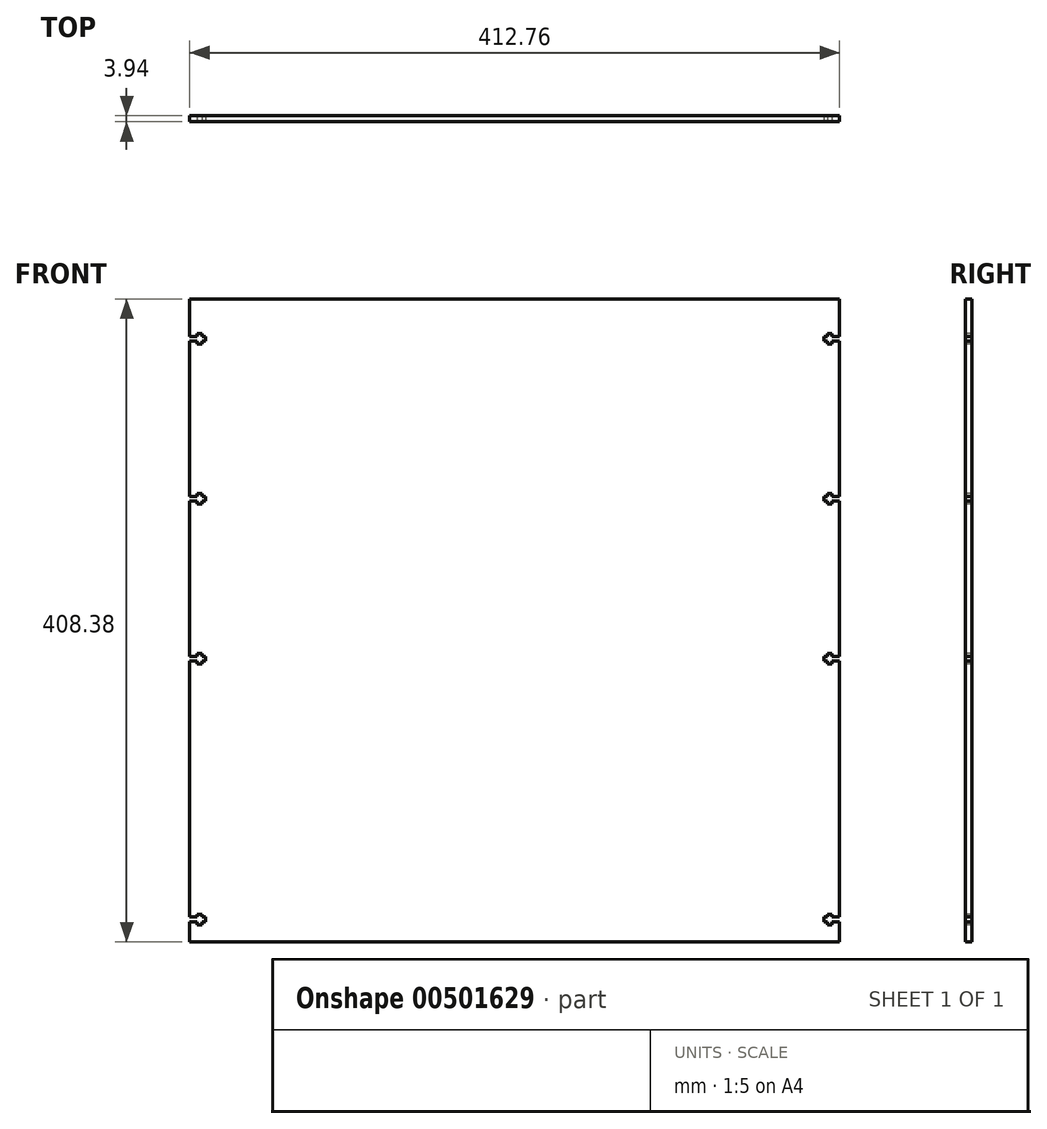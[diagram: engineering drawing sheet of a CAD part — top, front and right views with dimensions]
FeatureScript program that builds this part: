
annotation { "Feature Type Name" : "Feature", "Feature Type Description" : "" }
export const myFeature = defineFeature(function(context is Context, id is Id, definition is map)
    precondition{}
    {
        {
            var Q0;
            Q0=qCreatedBy(makeId("Front.planeOp"),FACE);
            var sketch = newSketch(context, id + "F0", { "sketchPlane" : qUnion([Q0])});
            skLineSegment(sketch, "E0.bottom", {"start": v(-206.38, 204.2) * mm, "end": v(206.38, 204.2) * mm});
            skLineSegment(sketch, "E0.top", {"start": v(-206.38, -204.2) * mm, "end": v(206.38, -204.2) * mm});
            skLineSegment(sketch, "E0.left", {"start": v(-206.38, 204.2) * mm, "end": v(-206.38, -204.2) * mm});
            skLineSegment(sketch, "E0.right", {"start": v(206.38, 204.2) * mm, "end": v(206.38, -204.2) * mm});
            skPoint(sketch, "E0.middle", {"position": v(0, 0) * mm});
            skSolve(sketch);
        }
        {
            var Q0;
            Q0=makeQuery(id+"F0.imprint","IMPRINT",FACE,{"disambiguationData":[TD([[makeQuery(id+"F0.imprint","IMPRINT",EDGE,{"derivedFrom":sQuery(id+"F0.wireOp",EDGE,"E0.bottom")}),-1.0]])]});
            extrude(context, id + "F1", {"entities" : qUnion([Q0]), "depth" : 3.94 * mm});
        }
        {
            var Q0;
            Q0=makeQuery(id+"F1.opExtrude","CAP_FACE",FACE,{"disambiguationData":[OSD([sQuery(id+"F0.wireOp",EDGE,"E0.bottom"),sQuery(id+"F0.wireOp",EDGE,"E0.top"),sQuery(id+"F0.wireOp",EDGE,"E0.left"),sQuery(id+"F0.wireOp",EDGE,"E0.right")])],"isStart":false});
            var sketch = newSketch(context, id + "F2", { "sketchPlane" : qUnion([Q0])});
            skLineSegment(sketch, "E1", {"start": v(-203.2, 178.8) * mm, "end": v(-196.34, 178.8) * mm, "construction": true});
            skLineSegment(sketch, "E2", {"start": v(-203.2, 177.32) * mm, "end": v(-201.6, 177.32) * mm});
            skLineSegment(sketch, "E3", {"start": v(-201.6, 177.32) * mm, "end": v(-201.6, 175.46) * mm});
            skLineSegment(sketch, "E4", {"start": v(-201.6, 175.46) * mm, "end": v(-198.57, 175.46) * mm});
            skLineSegment(sketch, "E5", {"start": v(-198.57, 175.46) * mm, "end": v(-198.57, 177.32) * mm});
            skLineSegment(sketch, "E6", {"start": v(-198.57, 177.32) * mm, "end": v(-196.34, 177.32) * mm});
            skLineSegment(sketch, "E7", {"start": v(-196.34, 177.32) * mm, "end": v(-196.34, 178.8) * mm});
            skLineSegment(sketch, "E8.MirrorCS", {"start": v(-201.6, 182.13) * mm, "end": v(-198.57, 182.13) * mm});
            skLineSegment(sketch, "E9.MirrorCS", {"start": v(-201.6, 180.27) * mm, "end": v(-201.6, 182.13) * mm});
            skLineSegment(sketch, "E10.MirrorCS", {"start": v(-203.2, 180.27) * mm, "end": v(-201.6, 180.27) * mm});
            skLineSegment(sketch, "E11.MirrorCS", {"start": v(-198.57, 182.13) * mm, "end": v(-198.57, 180.27) * mm});
            skLineSegment(sketch, "E12.MirrorCS", {"start": v(-198.57, 180.27) * mm, "end": v(-196.34, 180.27) * mm});
            skLineSegment(sketch, "E13.MirrorCS", {"start": v(-196.34, 180.27) * mm, "end": v(-196.34, 178.8) * mm});
            skLineSegment(sketch, "E14", {"start": v(-203.2, 180.27) * mm, "end": v(-203.2, 177.32) * mm});
            skLineSegment(sketch, "E15.bottom", {"start": v(-203.2, 180.27) * mm, "end": v(-206.38, 180.27) * mm});
            skLineSegment(sketch, "E15.top", {"start": v(-203.2, 177.32) * mm, "end": v(-206.38, 177.32) * mm});
            skLineSegment(sketch, "E15.right", {"start": v(-206.38, 180.27) * mm, "end": v(-206.38, 177.32) * mm});
            skLineSegment(sketch, "E16.0.1.0", {"start": v(-201.6, 80.53) * mm, "end": v(-198.57, 80.53) * mm});
            skLineSegment(sketch, "E16.0.1.1", {"start": v(-201.6, 78.67) * mm, "end": v(-201.6, 80.53) * mm});
            skLineSegment(sketch, "E16.0.1.2", {"start": v(-203.2, 78.67) * mm, "end": v(-201.6, 78.67) * mm});
            skLineSegment(sketch, "E16.0.1.3", {"start": v(-198.57, 80.53) * mm, "end": v(-198.57, 78.67) * mm});
            skLineSegment(sketch, "E16.0.1.4", {"start": v(-198.57, 78.67) * mm, "end": v(-196.34, 78.67) * mm});
            skLineSegment(sketch, "E16.0.1.5", {"start": v(-196.34, 78.67) * mm, "end": v(-196.34, 77.2) * mm});
            skLineSegment(sketch, "E16.0.1.6", {"start": v(-206.38, 78.67) * mm, "end": v(-206.38, 75.72) * mm});
            skLineSegment(sketch, "E16.0.1.7", {"start": v(-203.2, 78.67) * mm, "end": v(-206.38, 78.67) * mm});
            skLineSegment(sketch, "E16.0.1.8", {"start": v(-203.2, 75.72) * mm, "end": v(-206.38, 75.72) * mm});
            skLineSegment(sketch, "E16.0.1.9", {"start": v(-203.2, 77.2) * mm, "end": v(-196.34, 77.2) * mm, "construction": true});
            skLineSegment(sketch, "E16.0.1.10", {"start": v(-201.6, 75.72) * mm, "end": v(-201.6, 73.86) * mm});
            skLineSegment(sketch, "E16.0.1.11", {"start": v(-201.6, 73.86) * mm, "end": v(-198.57, 73.86) * mm});
            skLineSegment(sketch, "E16.0.1.12", {"start": v(-198.57, 73.86) * mm, "end": v(-198.57, 75.72) * mm});
            skLineSegment(sketch, "E16.0.1.13", {"start": v(-198.57, 75.72) * mm, "end": v(-196.34, 75.72) * mm});
            skLineSegment(sketch, "E16.0.1.14", {"start": v(-203.2, 75.72) * mm, "end": v(-201.6, 75.72) * mm});
            skLineSegment(sketch, "E16.0.1.15", {"start": v(-196.34, 75.72) * mm, "end": v(-196.34, 77.2) * mm});
            skLineSegment(sketch, "E16.0.1.16", {"start": v(-203.2, 78.67) * mm, "end": v(-203.2, 75.72) * mm});
            skLineSegment(sketch, "E16.0.1.17", {"start": v(-203.2, 78.67) * mm, "end": v(-203.2, 75.72) * mm});
            skLineSegment(sketch, "E16.0.2.0", {"start": v(-201.6, -21.07) * mm, "end": v(-198.57, -21.07) * mm});
            skLineSegment(sketch, "E16.0.2.1", {"start": v(-201.6, -22.93) * mm, "end": v(-201.6, -21.07) * mm});
            skLineSegment(sketch, "E16.0.2.2", {"start": v(-203.2, -22.93) * mm, "end": v(-201.6, -22.93) * mm});
            skLineSegment(sketch, "E16.0.2.3", {"start": v(-198.57, -21.07) * mm, "end": v(-198.57, -22.93) * mm});
            skLineSegment(sketch, "E16.0.2.4", {"start": v(-198.57, -22.93) * mm, "end": v(-196.34, -22.93) * mm});
            skLineSegment(sketch, "E16.0.2.5", {"start": v(-196.34, -22.93) * mm, "end": v(-196.34, -24.4) * mm});
            skLineSegment(sketch, "E16.0.2.6", {"start": v(-206.38, -22.93) * mm, "end": v(-206.38, -25.88) * mm});
            skLineSegment(sketch, "E16.0.2.7", {"start": v(-203.2, -22.93) * mm, "end": v(-206.38, -22.93) * mm});
            skLineSegment(sketch, "E16.0.2.8", {"start": v(-203.2, -25.88) * mm, "end": v(-206.38, -25.88) * mm});
            skLineSegment(sketch, "E16.0.2.9", {"start": v(-203.2, -24.4) * mm, "end": v(-196.34, -24.4) * mm, "construction": true});
            skLineSegment(sketch, "E16.0.2.10", {"start": v(-201.6, -25.88) * mm, "end": v(-201.6, -27.74) * mm});
            skLineSegment(sketch, "E16.0.2.11", {"start": v(-201.6, -27.74) * mm, "end": v(-198.57, -27.74) * mm});
            skLineSegment(sketch, "E16.0.2.12", {"start": v(-198.57, -27.74) * mm, "end": v(-198.57, -25.88) * mm});
            skLineSegment(sketch, "E16.0.2.13", {"start": v(-198.57, -25.88) * mm, "end": v(-196.34, -25.88) * mm});
            skLineSegment(sketch, "E16.0.2.14", {"start": v(-203.2, -25.88) * mm, "end": v(-201.6, -25.88) * mm});
            skLineSegment(sketch, "E16.0.2.15", {"start": v(-196.34, -25.88) * mm, "end": v(-196.34, -24.4) * mm});
            skLineSegment(sketch, "E16.0.2.16", {"start": v(-203.2, -22.93) * mm, "end": v(-203.2, -25.88) * mm});
            skLineSegment(sketch, "E16.0.2.17", {"start": v(-203.2, -22.93) * mm, "end": v(-203.2, -25.88) * mm});
            skLineSegment(sketch, "E16.direction1", {"start": v(-206.38, 177.32) * mm, "end": v(-180.98, 177.32) * mm, "construction": true});
            skLineSegment(sketch, "E16.direction2", {"start": v(-206.38, 177.32) * mm, "end": v(-206.38, 75.72) * mm, "construction": true});
            skLineSegment(sketch, "E17", {"start": v(-203.2, -189.9) * mm, "end": v(-196.34, -189.9) * mm, "construction": true});
            skLineSegment(sketch, "E18", {"start": v(-203.2, -191.38) * mm, "end": v(-201.6, -191.38) * mm});
            skLineSegment(sketch, "E19", {"start": v(-201.6, -191.38) * mm, "end": v(-201.6, -193.24) * mm});
            skLineSegment(sketch, "E20", {"start": v(-201.6, -193.24) * mm, "end": v(-198.57, -193.24) * mm});
            skLineSegment(sketch, "E21", {"start": v(-198.57, -193.24) * mm, "end": v(-198.57, -191.38) * mm});
            skLineSegment(sketch, "E22", {"start": v(-198.57, -191.38) * mm, "end": v(-196.34, -191.38) * mm});
            skLineSegment(sketch, "E23", {"start": v(-196.34, -191.38) * mm, "end": v(-196.34, -189.9) * mm});
            skLineSegment(sketch, "E24.MirrorCS", {"start": v(-201.6, -186.57) * mm, "end": v(-198.57, -186.57) * mm});
            skLineSegment(sketch, "E25.MirrorCS", {"start": v(-201.6, -188.43) * mm, "end": v(-201.6, -186.57) * mm});
            skLineSegment(sketch, "E26.MirrorCS", {"start": v(-203.2, -188.43) * mm, "end": v(-201.6, -188.43) * mm});
            skLineSegment(sketch, "E27.MirrorCS", {"start": v(-198.57, -186.57) * mm, "end": v(-198.57, -188.43) * mm});
            skLineSegment(sketch, "E28.MirrorCS", {"start": v(-198.57, -188.43) * mm, "end": v(-196.34, -188.43) * mm});
            skLineSegment(sketch, "E29.MirrorCS", {"start": v(-196.34, -188.43) * mm, "end": v(-196.34, -189.9) * mm});
            skLineSegment(sketch, "E30", {"start": v(-203.2, -188.43) * mm, "end": v(-203.2, -191.38) * mm});
            skLineSegment(sketch, "E31.bottom", {"start": v(-203.2, -188.43) * mm, "end": v(-206.38, -188.43) * mm});
            skLineSegment(sketch, "E31.top", {"start": v(-203.2, -191.38) * mm, "end": v(-206.38, -191.38) * mm});
            skLineSegment(sketch, "E31.right", {"start": v(-206.38, -188.43) * mm, "end": v(-206.38, -191.38) * mm});
            skLineSegment(sketch, "E32.MirrorCS", {"start": v(203.2, 180.27) * mm, "end": v(203.2, 177.32) * mm});
            skLineSegment(sketch, "E33.MirrorCS", {"start": v(196.34, -188.43) * mm, "end": v(196.34, -189.9) * mm});
            skLineSegment(sketch, "E34.MirrorCS", {"start": v(201.6, -193.24) * mm, "end": v(198.57, -193.24) * mm});
            skLineSegment(sketch, "E35.MirrorCS", {"start": v(201.6, -186.57) * mm, "end": v(198.57, -186.57) * mm});
            skLineSegment(sketch, "E36.MirrorCS", {"start": v(201.6, -188.43) * mm, "end": v(201.6, -186.57) * mm});
            skLineSegment(sketch, "E37.MirrorCS", {"start": v(203.2, 177.32) * mm, "end": v(201.6, 177.32) * mm});
            skLineSegment(sketch, "E38.MirrorCS", {"start": v(201.6, 177.32) * mm, "end": v(201.6, 175.46) * mm});
            skLineSegment(sketch, "E39.MirrorCS", {"start": v(198.57, 177.32) * mm, "end": v(196.34, 177.32) * mm});
            skLineSegment(sketch, "E40.MirrorCS", {"start": v(196.34, 177.32) * mm, "end": v(196.34, 178.8) * mm});
            skLineSegment(sketch, "E41.MirrorCS", {"start": v(203.2, -188.43) * mm, "end": v(203.2, -191.38) * mm});
            skLineSegment(sketch, "E42.MirrorCS", {"start": v(201.6, 182.13) * mm, "end": v(198.57, 182.13) * mm});
            skLineSegment(sketch, "E43.MirrorCS", {"start": v(198.57, -191.38) * mm, "end": v(196.34, -191.38) * mm});
            skLineSegment(sketch, "E44.MirrorCS", {"start": v(198.57, -186.57) * mm, "end": v(198.57, -188.43) * mm});
            skLineSegment(sketch, "E45.MirrorCS", {"start": v(198.57, 75.72) * mm, "end": v(196.34, 75.72) * mm});
            skLineSegment(sketch, "E46.MirrorCS", {"start": v(203.2, -188.43) * mm, "end": v(206.38, -188.43) * mm});
            skLineSegment(sketch, "E47.MirrorCS", {"start": v(203.2, -191.38) * mm, "end": v(206.38, -191.38) * mm});
            skLineSegment(sketch, "E48.MirrorCS", {"start": v(201.6, 175.46) * mm, "end": v(198.57, 175.46) * mm});
            skLineSegment(sketch, "E49.MirrorCS", {"start": v(201.6, 180.27) * mm, "end": v(201.6, 182.13) * mm});
            skLineSegment(sketch, "E50.MirrorCS", {"start": v(203.2, 180.27) * mm, "end": v(201.6, 180.27) * mm});
            skLineSegment(sketch, "E51.MirrorCS", {"start": v(198.57, -193.24) * mm, "end": v(198.57, -191.38) * mm});
            skLineSegment(sketch, "E52.MirrorCS", {"start": v(203.2, -191.38) * mm, "end": v(201.6, -191.38) * mm});
            skLineSegment(sketch, "E53.MirrorCS", {"start": v(196.34, 180.27) * mm, "end": v(196.34, 178.8) * mm});
            skLineSegment(sketch, "E54.MirrorCS", {"start": v(203.2, 78.67) * mm, "end": v(201.6, 78.67) * mm});
            skLineSegment(sketch, "E55.MirrorCS", {"start": v(203.2, 78.67) * mm, "end": v(203.2, 75.72) * mm});
            skLineSegment(sketch, "E56.MirrorCS", {"start": v(203.2, -189.9) * mm, "end": v(196.34, -189.9) * mm, "construction": true});
            skLineSegment(sketch, "E57.MirrorCS", {"start": v(198.57, -22.93) * mm, "end": v(196.34, -22.93) * mm});
            skLineSegment(sketch, "E58.MirrorCS", {"start": v(203.2, -22.93) * mm, "end": v(201.6, -22.93) * mm});
            skLineSegment(sketch, "E59.MirrorCS", {"start": v(198.57, 78.67) * mm, "end": v(196.34, 78.67) * mm});
            skLineSegment(sketch, "E60.MirrorCS", {"start": v(203.2, 180.27) * mm, "end": v(206.38, 180.27) * mm});
            skLineSegment(sketch, "E61.MirrorCS", {"start": v(203.2, 177.32) * mm, "end": v(206.38, 177.32) * mm});
            skLineSegment(sketch, "E62.MirrorCS", {"start": v(206.38, 180.27) * mm, "end": v(206.38, 177.32) * mm});
            skLineSegment(sketch, "E63.MirrorCS", {"start": v(196.34, 78.67) * mm, "end": v(196.34, 77.2) * mm});
            skLineSegment(sketch, "E64.MirrorCS", {"start": v(203.2, -188.43) * mm, "end": v(201.6, -188.43) * mm});
            skLineSegment(sketch, "E65.MirrorCS", {"start": v(201.6, -191.38) * mm, "end": v(201.6, -193.24) * mm});
            skLineSegment(sketch, "E66.MirrorCS", {"start": v(198.57, -188.43) * mm, "end": v(196.34, -188.43) * mm});
            skLineSegment(sketch, "E67.MirrorCS", {"start": v(203.2, 178.8) * mm, "end": v(196.34, 178.8) * mm, "construction": true});
            skLineSegment(sketch, "E68.MirrorCS", {"start": v(198.57, 175.46) * mm, "end": v(198.57, 177.32) * mm});
            skLineSegment(sketch, "E69.MirrorCS", {"start": v(196.34, -191.38) * mm, "end": v(196.34, -189.9) * mm});
            skLineSegment(sketch, "E70.MirrorCS", {"start": v(198.57, 80.53) * mm, "end": v(198.57, 78.67) * mm});
            skLineSegment(sketch, "E71.MirrorCS", {"start": v(198.57, 182.13) * mm, "end": v(198.57, 180.27) * mm});
            skLineSegment(sketch, "E72.MirrorCS", {"start": v(198.57, 180.27) * mm, "end": v(196.34, 180.27) * mm});
            skLineSegment(sketch, "E73.MirrorCS", {"start": v(206.38, -188.43) * mm, "end": v(206.38, -191.38) * mm});
            skLineSegment(sketch, "E74.MirrorCS", {"start": v(203.2, -22.93) * mm, "end": v(203.2, -25.88) * mm});
            skLineSegment(sketch, "E75.MirrorCS", {"start": v(201.6, 73.86) * mm, "end": v(198.57, 73.86) * mm});
            skLineSegment(sketch, "E76.MirrorCS", {"start": v(201.6, 80.53) * mm, "end": v(198.57, 80.53) * mm});
            skLineSegment(sketch, "E77.MirrorCS", {"start": v(203.2, -25.88) * mm, "end": v(201.6, -25.88) * mm});
            skLineSegment(sketch, "E78.MirrorCS", {"start": v(198.57, -25.88) * mm, "end": v(196.34, -25.88) * mm});
            skLineSegment(sketch, "E79.MirrorCS", {"start": v(196.34, 75.72) * mm, "end": v(196.34, 77.2) * mm});
            skLineSegment(sketch, "E80.MirrorCS", {"start": v(196.34, -25.88) * mm, "end": v(196.34, -24.4) * mm});
            skLineSegment(sketch, "E81.MirrorCS", {"start": v(203.2, 75.72) * mm, "end": v(201.6, 75.72) * mm});
            skLineSegment(sketch, "E82.MirrorCS", {"start": v(201.6, -25.88) * mm, "end": v(201.6, -27.74) * mm});
            skLineSegment(sketch, "E83.MirrorCS", {"start": v(201.6, 75.72) * mm, "end": v(201.6, 73.86) * mm});
            skLineSegment(sketch, "E84.MirrorCS", {"start": v(201.6, -21.07) * mm, "end": v(198.57, -21.07) * mm});
            skLineSegment(sketch, "E85.MirrorCS", {"start": v(206.38, 78.67) * mm, "end": v(206.38, 75.72) * mm});
            skLineSegment(sketch, "E86.MirrorCS", {"start": v(201.6, -27.74) * mm, "end": v(198.57, -27.74) * mm});
            skLineSegment(sketch, "E87.MirrorCS", {"start": v(198.57, -27.74) * mm, "end": v(198.57, -25.88) * mm});
            skLineSegment(sketch, "E88.MirrorCS", {"start": v(198.57, -21.07) * mm, "end": v(198.57, -22.93) * mm});
            skLineSegment(sketch, "E89.MirrorCS", {"start": v(206.38, -22.93) * mm, "end": v(206.38, -25.88) * mm});
            skLineSegment(sketch, "E90.MirrorCS", {"start": v(203.2, 75.72) * mm, "end": v(206.38, 75.72) * mm});
            skLineSegment(sketch, "E91.MirrorCS", {"start": v(201.6, 78.67) * mm, "end": v(201.6, 80.53) * mm});
            skLineSegment(sketch, "E92.MirrorCS", {"start": v(201.6, -22.93) * mm, "end": v(201.6, -21.07) * mm});
            skLineSegment(sketch, "E93.MirrorCS", {"start": v(198.57, 73.86) * mm, "end": v(198.57, 75.72) * mm});
            skLineSegment(sketch, "E94.MirrorCS", {"start": v(203.2, -25.88) * mm, "end": v(206.38, -25.88) * mm});
            skLineSegment(sketch, "E95.MirrorCS", {"start": v(203.2, -24.4) * mm, "end": v(196.34, -24.4) * mm, "construction": true});
            skLineSegment(sketch, "E96.MirrorCS", {"start": v(196.34, -22.93) * mm, "end": v(196.34, -24.4) * mm});
            skLineSegment(sketch, "E97.MirrorCS", {"start": v(203.2, 78.67) * mm, "end": v(206.38, 78.67) * mm});
            skLineSegment(sketch, "E98.MirrorCS", {"start": v(203.2, 77.2) * mm, "end": v(196.34, 77.2) * mm, "construction": true});
            skLineSegment(sketch, "E99.MirrorCS", {"start": v(203.2, -22.93) * mm, "end": v(206.38, -22.93) * mm});
            skLineSegment(sketch, "E100.MirrorCS", {"start": v(206.38, 177.32) * mm, "end": v(180.98, 177.32) * mm, "construction": true});
            skLineSegment(sketch, "E101.MirrorCS", {"start": v(206.38, 177.32) * mm, "end": v(206.38, 75.72) * mm, "construction": true});
            skSolve(sketch);
        }
        {
            var Q0;
            Q0=qSketchRegion(id+"F2",true);
            var Q1;
            Q1=makeQuery(id+"F1.opExtrude","CAP_FACE",FACE,{"disambiguationData":[OSD([sQuery(id+"F0.wireOp",EDGE,"E0.bottom"),sQuery(id+"F0.wireOp",EDGE,"E0.top"),sQuery(id+"F0.wireOp",EDGE,"E0.left"),sQuery(id+"F0.wireOp",EDGE,"E0.right")])],"isStart":true});
            extrude(context, id + "F3", {"entities" : qUnion([Q0]), "operationType" : NewBodyOperationType.REMOVE, "endBound" : BoundingType.UP_TO_SURFACE, "oppositeDirection" : true, "endBoundEntityFace" : qUnion([Q1]), "depth" : 25.4 * mm});
        }
    });
